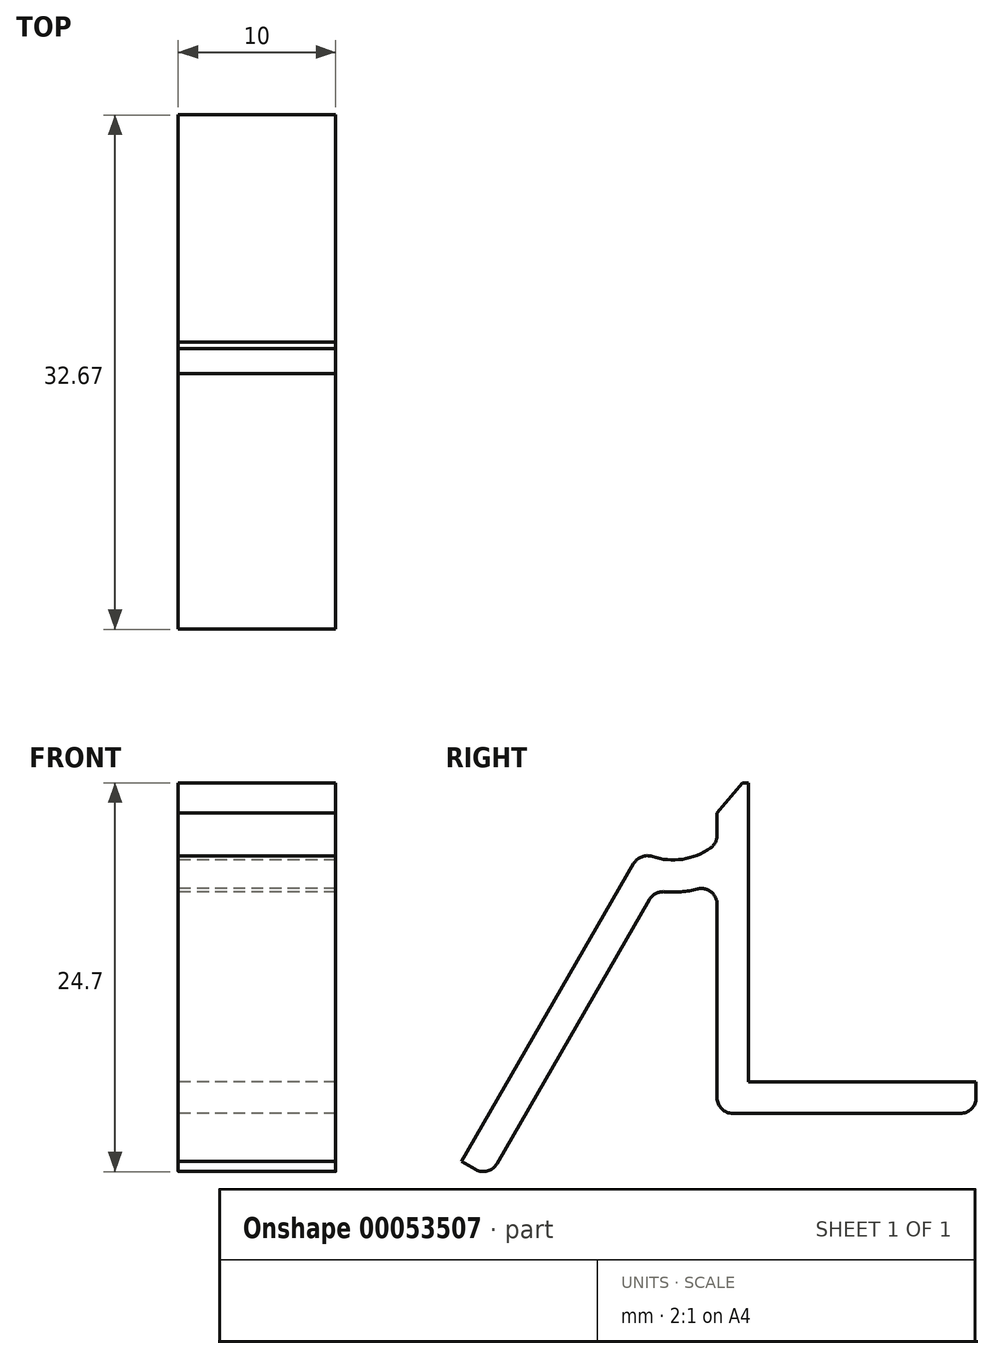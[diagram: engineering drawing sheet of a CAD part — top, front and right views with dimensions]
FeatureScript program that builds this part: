
annotation { "Feature Type Name" : "Feature", "Feature Type Description" : "" }
export const myFeature = defineFeature(function(context is Context, id is Id, definition is map)
    precondition{}
    {
        {
            var Q0;
            Q0=qCreatedBy(makeId("Right.planeOp"),FACE);
            var sketch = newSketch(context, id + "F0", { "sketchPlane" : qUnion([Q0])});
            skLineSegment(sketch, "E0.bottom", {"start": v(-0.5, 35) * mm, "end": v(-4.5, 35) * mm});
            skLineSegment(sketch, "E0.top", {"start": v(-0.5, 0) * mm, "end": v(-4.5, 0) * mm});
            skLineSegment(sketch, "E0.left", {"start": v(0, 34.5) * mm, "end": v(0, 0.5) * mm});
            skLineSegment(sketch, "E0.right", {"start": v(-5, 34.5) * mm, "end": v(-5, 0.5) * mm});
            skPoint(sketch, "E1.visualSharp", {"position": v(0, 35) * mm});
            skArc(sketch, "E1.filletArc", {"start": v(0, 34.5) * mm, "mid": v(-0.15, 34.85) * mm, "end": v(-0.5, 35) * mm});
            skPoint(sketch, "E2.visualSharp", {"position": v(-5, 35) * mm});
            skArc(sketch, "E2.filletArc", {"start": v(-4.5, 35) * mm, "mid": v(-4.85, 34.85) * mm, "end": v(-5, 34.5) * mm});
            skPoint(sketch, "E3.visualSharp", {"position": v(-5, 0) * mm});
            skArc(sketch, "E3.filletArc", {"start": v(-5, 0.5) * mm, "mid": v(-4.85, 0.15) * mm, "end": v(-4.5, 0) * mm});
            skPoint(sketch, "E4.visualSharp", {"position": v(0, 0) * mm});
            skArc(sketch, "E4.filletArc", {"start": v(-0.5, 0) * mm, "mid": v(-0.15, 0.15) * mm, "end": v(0, 0.5) * mm});
            skLineSegment(sketch, "E5", {"start": v(-5, 17.5) * mm, "end": v(0, 17.5) * mm, "construction": true});
            skLineSegment(sketch, "E6.rect.bottom", {"start": v(-2.5, 36) * mm, "end": v(-2.5, 36) * mm});
            skLineSegment(sketch, "E6.rect.top", {"start": v(-1.5, 34) * mm, "end": v(-3.5, 34) * mm, "construction": true});
            skLineSegment(sketch, "E6.rect.left", {"start": v(-1.5, 35) * mm, "end": v(-1.5, 34) * mm, "construction": true});
            skLineSegment(sketch, "E6.rect.right", {"start": v(-3.5, 35) * mm, "end": v(-3.5, 34) * mm, "construction": true});
            skPoint(sketch, "E6.rect.middle", {"position": v(-2.5, 35) * mm});
            skPoint(sketch, "E7.visualSharp", {"position": v(-3.5, 36) * mm});
            skArc(sketch, "E7.filletArc", {"start": v(-2.5, 36) * mm, "mid": v(-3.2, 35.7) * mm, "end": v(-3.5, 35) * mm, "construction": true});
            skPoint(sketch, "E8.visualSharp", {"position": v(-1.5, 36) * mm});
            skArc(sketch, "E8.filletArc", {"start": v(-1.5, 35) * mm, "mid": v(-1.8, 35.7) * mm, "end": v(-2.5, 36) * mm, "construction": true});
            skPoint(sketch, "E9.MirrorP", {"position": v(-2.5, 0) * mm});
            skPoint(sketch, "E10.MirrorP", {"position": v(-1.5, -1) * mm});
            skArc(sketch, "E11.MirrorCS", {"start": v(-1.5, 0) * mm, "mid": v(-1.8, -0.7) * mm, "end": v(-2.5, -1) * mm, "construction": true});
            skPoint(sketch, "E12.MirrorP", {"position": v(-3.5, -1) * mm});
            skLineSegment(sketch, "E13.MirrorCS", {"start": v(-2.5, -1) * mm, "end": v(-2.5, -1) * mm});
            skArc(sketch, "E14.MirrorCS", {"start": v(-2.5, -1) * mm, "mid": v(-3.2, -0.7) * mm, "end": v(-3.5, 0) * mm, "construction": true});
            skLineSegment(sketch, "E15.MirrorCS", {"start": v(-3.5, 0) * mm, "end": v(-3.5, 1) * mm, "construction": true});
            skLineSegment(sketch, "E16.MirrorCS", {"start": v(-1.5, 1) * mm, "end": v(-3.5, 1) * mm, "construction": true});
            skLineSegment(sketch, "E17.MirrorCS", {"start": v(-1.5, 0) * mm, "end": v(-1.5, 1) * mm, "construction": true});
            skLineSegment(sketch, "E18.rect.bottom", {"start": v(-4.5, 29.4) * mm, "end": v(-5, 29.4) * mm});
            skLineSegment(sketch, "E18.rect.top", {"start": v(-4.5, 5.6) * mm, "end": v(-5, 5.6) * mm});
            skLineSegment(sketch, "E18.rect.left", {"start": v(-4.5, 29.4) * mm, "end": v(-4.5, 5.6) * mm, "construction": true});
            skPoint(sketch, "E18.rect.middle", {"position": v(-5, 17.5) * mm});
            skPoint(sketch, "E18.rect.right.end.orphan", {"position": v(-5.5, 5.6) * mm});
            skPoint(sketch, "E18.rect.right.start.orphan", {"position": v(-5.5, 29.4) * mm});
            skSolve(sketch);
        }
        {
            var Q0;
            Q0=qCreatedBy(makeId("Right.planeOp"),FACE);
            var sketch = newSketch(context, id + "F1", { "sketchPlane" : qUnion([Q0])});
            skLineSegment(sketch, "E19", {"start": v(-4.2, 35.5) * mm, "end": v(-3.8, 35.5) * mm});
            skLineSegment(sketch, "E20", {"start": v(0, 35.2) * mm, "end": v(0, -0.2) * mm});
            skLineSegment(sketch, "E21", {"start": v(-0.3, -0.5) * mm, "end": v(-1.2, -0.5) * mm});
            skLineSegment(sketch, "E22", {"start": v(-4.5, -0.8) * mm, "end": v(-4.5, -1.5) * mm});
            skLineSegment(sketch, "E23", {"start": v(-3.5, -2.5) * mm, "end": v(2.68, -2.5) * mm, "construction": true});
            skLineSegment(sketch, "E24", {"start": v(-4.5, 35.8) * mm, "end": v(-4.5, 36.5) * mm});
            skLineSegment(sketch, "E25", {"start": v(-3.5, 37.5) * mm, "end": v(0.9, 37.5) * mm});
            skLineSegment(sketch, "E26", {"start": v(-3.5, 35.8) * mm, "end": v(-3.5, 36.05) * mm});
            skLineSegment(sketch, "E27", {"start": v(-3.5, 36.05) * mm, "end": v(-1.5, 36.05) * mm});
            skLineSegment(sketch, "E28", {"start": v(-1.5, 36.05) * mm, "end": v(-1.5, 35.8) * mm});
            skLineSegment(sketch, "E29.trimOffspring", {"start": v(-1.2, 35.5) * mm, "end": v(-0.3, 35.5) * mm});
            skLineSegment(sketch, "E30.MirrorCS", {"start": v(-1.5, -1.05) * mm, "end": v(-1.5, -0.8) * mm});
            skLineSegment(sketch, "E31.MirrorCS", {"start": v(-3.5, -0.8) * mm, "end": v(-3.5, -1.05) * mm});
            skLineSegment(sketch, "E32.MirrorCS", {"start": v(-3.5, -1.05) * mm, "end": v(-1.5, -1.05) * mm});
            skLineSegment(sketch, "E33.trimOffspring", {"start": v(-3.8, -0.5) * mm, "end": v(-4.2, -0.5) * mm});
            skPoint(sketch, "E34.visualSharp", {"position": v(-4.5, 35.5) * mm});
            skArc(sketch, "E34.filletArc", {"start": v(-4.5, 35.8) * mm, "mid": v(-4.41, 35.59) * mm, "end": v(-4.2, 35.5) * mm});
            skPoint(sketch, "E35.visualSharp", {"position": v(-3.5, 35.5) * mm});
            skArc(sketch, "E35.filletArc", {"start": v(-3.8, 35.5) * mm, "mid": v(-3.59, 35.59) * mm, "end": v(-3.5, 35.8) * mm});
            skPoint(sketch, "E36.visualSharp", {"position": v(0, 35.5) * mm});
            skArc(sketch, "E36.filletArc", {"start": v(0, 35.2) * mm, "mid": v(-0.09, 35.41) * mm, "end": v(-0.3, 35.5) * mm});
            skPoint(sketch, "E37.visualSharp", {"position": v(-1.5, 35.5) * mm});
            skArc(sketch, "E37.filletArc", {"start": v(-1.5, 35.8) * mm, "mid": v(-1.41, 35.59) * mm, "end": v(-1.2, 35.5) * mm});
            skPoint(sketch, "E38.visualSharp", {"position": v(-4.5, -0.5) * mm});
            skArc(sketch, "E38.filletArc", {"start": v(-4.2, -0.5) * mm, "mid": v(-4.41, -0.59) * mm, "end": v(-4.5, -0.8) * mm});
            skPoint(sketch, "E39.visualSharp", {"position": v(-3.5, -0.5) * mm});
            skArc(sketch, "E39.filletArc", {"start": v(-3.5, -0.8) * mm, "mid": v(-3.59, -0.59) * mm, "end": v(-3.8, -0.5) * mm});
            skPoint(sketch, "E40.visualSharp", {"position": v(-1.5, -0.5) * mm});
            skArc(sketch, "E40.filletArc", {"start": v(-1.2, -0.5) * mm, "mid": v(-1.41, -0.59) * mm, "end": v(-1.5, -0.8) * mm});
            skPoint(sketch, "E41.visualSharp", {"position": v(0, -0.5) * mm});
            skArc(sketch, "E41.filletArc", {"start": v(-0.3, -0.5) * mm, "mid": v(-0.09, -0.41) * mm, "end": v(0, -0.2) * mm});
            skArc(sketch, "E42", {"start": v(1.17, 37.07) * mm, "mid": v(2.4, 34.28) * mm, "end": v(4.95, 35.94) * mm});
            skArc(sketch, "E43", {"start": v(3.77, 32.28) * mm, "mid": v(5.44, 33.05) * mm, "end": v(6.58, 34.49) * mm});
            skLineSegment(sketch, "E44", {"start": v(5.5, 36.2) * mm, "end": v(5.25, 36.2) * mm});
            skPoint(sketch, "E45.visualSharp", {"position": v(1.45, 37.5) * mm});
            skArc(sketch, "E45.filletArc", {"start": v(1.17, 37.07) * mm, "mid": v(1.15, 37.36) * mm, "end": v(0.9, 37.5) * mm});
            skPoint(sketch, "E46.visualSharp", {"position": v(4.97, 36.2) * mm});
            skArc(sketch, "E46.filletArc", {"start": v(5.25, 36.2) * mm, "mid": v(5.05, 36.13) * mm, "end": v(4.95, 35.94) * mm});
            skPoint(sketch, "E47.visualSharp", {"position": v(6.97, 36.2) * mm});
            skArc(sketch, "E47.filletArc", {"start": v(6.58, 34.49) * mm, "mid": v(6.51, 35.64) * mm, "end": v(5.5, 36.2) * mm});
            skPoint(sketch, "E48.visualSharp", {"position": v(2.97, 32.2) * mm});
            skArc(sketch, "E48.filletArc", {"start": v(3.77, 32.28) * mm, "mid": v(3.2, 31.93) * mm, "end": v(2.97, 31.3) * mm});
            skPoint(sketch, "E49.visualSharp", {"position": v(-4.5, 37.5) * mm});
            skArc(sketch, "E49.filletArc", {"start": v(-3.5, 37.5) * mm, "mid": v(-4.2, 37.2) * mm, "end": v(-4.5, 36.5) * mm});
            skPoint(sketch, "E50.visualSharp", {"position": v(-4.5, -2.5) * mm});
            skArc(sketch, "E50.filletArc", {"start": v(-4.5, -1.5) * mm, "mid": v(-4.26, -2.15) * mm, "end": v(-3.65, -2.49) * mm});
            skArc(sketch, "E51", {"start": v(4.02, -3.14) * mm, "mid": v(-6.12, -2.09) * mm, "end": v(-15.65, 1.53) * mm, "construction": true});
            skLineSegment(sketch, "E52", {"start": v(-3.65, -2.49) * mm, "end": v(-1.02, -2.88) * mm});
            skArc(sketch, "E53", {"start": v(-0.25, -3.48) * mm, "mid": v(0.31, -3.85) * mm, "end": v(0.86, -3.47) * mm});
            skLineSegment(sketch, "E54", {"start": v(1.48, -2.9) * mm, "end": v(4.66, -1.84) * mm});
            skPoint(sketch, "E55.visualSharp", {"position": v(-0.23, -3) * mm});
            skArc(sketch, "E55.filletArc", {"start": v(-0.25, -3.48) * mm, "mid": v(-0.55, -3.08) * mm, "end": v(-1.02, -2.88) * mm});
            skPoint(sketch, "E56.visualSharp", {"position": v(0.89, -3.1) * mm});
            skArc(sketch, "E56.filletArc", {"start": v(1.48, -2.9) * mm, "mid": v(1.1, -3.12) * mm, "end": v(0.86, -3.47) * mm});
            skPoint(sketch, "E57.visualSharp", {"position": v(2.68, -2.5) * mm});
            skLineSegment(sketch, "E58", {"start": v(6.7, 35) * mm, "end": v(6.7, -7.44) * mm, "construction": true});
            skLineSegment(sketch, "E59", {"start": v(4.5, 9.3) * mm, "end": v(3.17, 9.3) * mm});
            skPoint(sketch, "E60.visualSharp", {"position": v(6.7, 9.3) * mm});
            skLineSegment(sketch, "E61.trimOffspring", {"start": v(2.97, 9.5) * mm, "end": v(2.97, 31.3) * mm});
            skPoint(sketch, "E62.visualSharp", {"position": v(6.7, 6.12) * mm});
            skPoint(sketch, "E63.visualSharp", {"position": v(2.97, 9.3) * mm});
            skArc(sketch, "E63.filletArc", {"start": v(2.97, 9.5) * mm, "mid": v(3.03, 9.36) * mm, "end": v(3.17, 9.3) * mm});
            skLineSegment(sketch, "E64", {"start": v(5, 8.8) * mm, "end": v(5, 7.85) * mm});
            skLineSegment(sketch, "E65", {"start": v(4.5, 7.35) * mm, "end": v(4.37, 7.35) * mm});
            skLineSegment(sketch, "E66", {"start": v(3, 7.35) * mm, "end": v(3, -0.65) * mm});
            skLineSegment(sketch, "E67", {"start": v(4.37, -0.65) * mm, "end": v(4.5, -0.65) * mm});
            skArc(sketch, "E68", {"start": v(3, 7.35) * mm, "mid": v(3.37, 7.84) * mm, "end": v(3.93, 7.6) * mm});
            skArc(sketch, "E69", {"start": v(3, -0.65) * mm, "mid": v(3.37, -1.13) * mm, "end": v(3.93, -0.9) * mm});
            skPoint(sketch, "E70.visualSharp", {"position": v(4, 7.35) * mm});
            skArc(sketch, "E70.filletArc", {"start": v(3.93, 7.6) * mm, "mid": v(4.12, 7.42) * mm, "end": v(4.37, 7.35) * mm});
            skPoint(sketch, "E71.newPointA", {"position": v(5, 7.35) * mm});
            skArc(sketch, "E71.filletArc", {"start": v(4.5, 7.35) * mm, "mid": v(4.85, 7.5) * mm, "end": v(5, 7.85) * mm});
            skPoint(sketch, "E72.visualSharp", {"position": v(4, -0.65) * mm});
            skArc(sketch, "E72.filletArc", {"start": v(4.37, -0.65) * mm, "mid": v(4.12, -0.71) * mm, "end": v(3.93, -0.9) * mm});
            skLineSegment(sketch, "E73", {"start": v(5, -1.15) * mm, "end": v(5, -1.37) * mm});
            skPoint(sketch, "E74.visualSharp", {"position": v(5, -0.65) * mm});
            skArc(sketch, "E74.filletArc", {"start": v(5, -1.15) * mm, "mid": v(4.85, -0.8) * mm, "end": v(4.5, -0.65) * mm});
            skPoint(sketch, "E75.visualSharp", {"position": v(5, -1.73) * mm});
            skArc(sketch, "E75.filletArc", {"start": v(4.66, -1.84) * mm, "mid": v(4.9, -1.66) * mm, "end": v(5, -1.37) * mm});
            skPoint(sketch, "E76.visualSharp", {"position": v(5, 9.3) * mm});
            skArc(sketch, "E76.filletArc", {"start": v(5, 8.8) * mm, "mid": v(4.85, 9.15) * mm, "end": v(4.5, 9.3) * mm});
            skSolve(sketch);
        }
        {
            var Q0;
            Q0=qCreatedBy(makeId("Right.planeOp"),FACE);
            var sketch = newSketch(context, id + "F2", { "sketchPlane" : qUnion([Q0])});
            skLineSegment(sketch, "E77", {"start": v(7.77, 37) * mm, "end": v(7.77, 18) * mm});
            skLineSegment(sketch, "E78", {"start": v(7.77, 37) * mm, "end": v(7.37, 37) * mm});
            skArc(sketch, "E79.0", {"start": v(1.65, 32.32) * mm, "mid": v(3.57, 32.14) * mm, "end": v(5.35, 32.86) * mm});
            skLineSegment(sketch, "E80", {"start": v(3.07, 9.8) * mm, "end": v(5.07, 9.8) * mm});
            skLineSegment(sketch, "E81", {"start": v(6.77, 16) * mm, "end": v(21.21, 16) * mm});
            skLineSegment(sketch, "E82", {"start": v(22.21, 17) * mm, "end": v(22.21, 18) * mm});
            skPoint(sketch, "E83.visualSharp", {"position": v(7.37, 37) * mm});
            skPoint(sketch, "E84.visualSharp", {"position": v(22.21, 16) * mm});
            skPoint(sketch, "E85.orphan", {"position": v(0, 33.37) * mm});
            skArc(sketch, "E86.0", {"start": v(2.43, 30.08) * mm, "mid": v(3.48, 30.08) * mm, "end": v(4.52, 30.25) * mm});
            skLineSegment(sketch, "E86.1", {"start": v(1.48, 29.58) * mm, "end": v(-8.2, 12.8) * mm});
            skLineSegment(sketch, "E87", {"start": v(-10.46, 12.95) * mm, "end": v(-9.57, 12.44) * mm});
            skPoint(sketch, "E88.visualSharp", {"position": v(-8.7, 11.94) * mm});
            skArc(sketch, "E88.filletArc", {"start": v(-9.57, 12.44) * mm, "mid": v(-8.82, 12.34) * mm, "end": v(-8.2, 12.8) * mm});
            skPoint(sketch, "E89.visualSharp", {"position": v(1.81, 30.17) * mm});
            skArc(sketch, "E89.filletArc", {"start": v(2.43, 30.08) * mm, "mid": v(1.88, 29.97) * mm, "end": v(1.48, 29.58) * mm});
            skPoint(sketch, "E90.visualSharp", {"position": v(0.92, 32.65) * mm});
            skArc(sketch, "E90.filletArc", {"start": v(1.65, 32.32) * mm, "mid": v(0.98, 32.3) * mm, "end": v(0.47, 31.87) * mm});
            skLineSegment(sketch, "E91", {"start": v(5.77, 35.1) * mm, "end": v(5.77, 33.68) * mm});
            skLineSegment(sketch, "E92", {"start": v(0.47, 31.87) * mm, "end": v(-10.46, 12.95) * mm});
            skLineSegment(sketch, "E93.trimOffspring", {"start": v(5.77, 29.29) * mm, "end": v(5.77, 17) * mm});
            skLineSegment(sketch, "E94", {"start": v(2.97, 36.2) * mm, "end": v(2.97, 34.14) * mm, "construction": true});
            skLineSegment(sketch, "E95", {"start": v(7.37, 37) * mm, "end": v(5.77, 35.1) * mm});
            skPoint(sketch, "E96.visualSharp", {"position": v(5.77, 16) * mm});
            skArc(sketch, "E96.filletArc", {"start": v(5.77, 17) * mm, "mid": v(6.06, 16.3) * mm, "end": v(6.77, 16) * mm});
            skArc(sketch, "E97.filletArc", {"start": v(21.21, 16) * mm, "mid": v(21.92, 16.3) * mm, "end": v(22.21, 17) * mm});
            skPoint(sketch, "E98.visualSharp", {"position": v(5.77, 30.73) * mm});
            skArc(sketch, "E98.filletArc", {"start": v(5.77, 29.29) * mm, "mid": v(5.38, 30.08) * mm, "end": v(4.52, 30.25) * mm});
            skPoint(sketch, "E99.visualSharp", {"position": v(5.77, 33.2) * mm});
            skArc(sketch, "E99.filletArc", {"start": v(5.35, 32.86) * mm, "mid": v(5.66, 33.22) * mm, "end": v(5.77, 33.68) * mm});
            skLineSegment(sketch, "E100", {"start": v(22.21, 18) * mm, "end": v(7.77, 18) * mm});
            skSolve(sketch);
        }
        {
            var Q0;
            Q0 = qSketchRegion(id + "F2", true);
            extrude(context, id + "F3", {"entities" : qUnion([Q0]), "depth" : 10 * mm});
        }
    });
